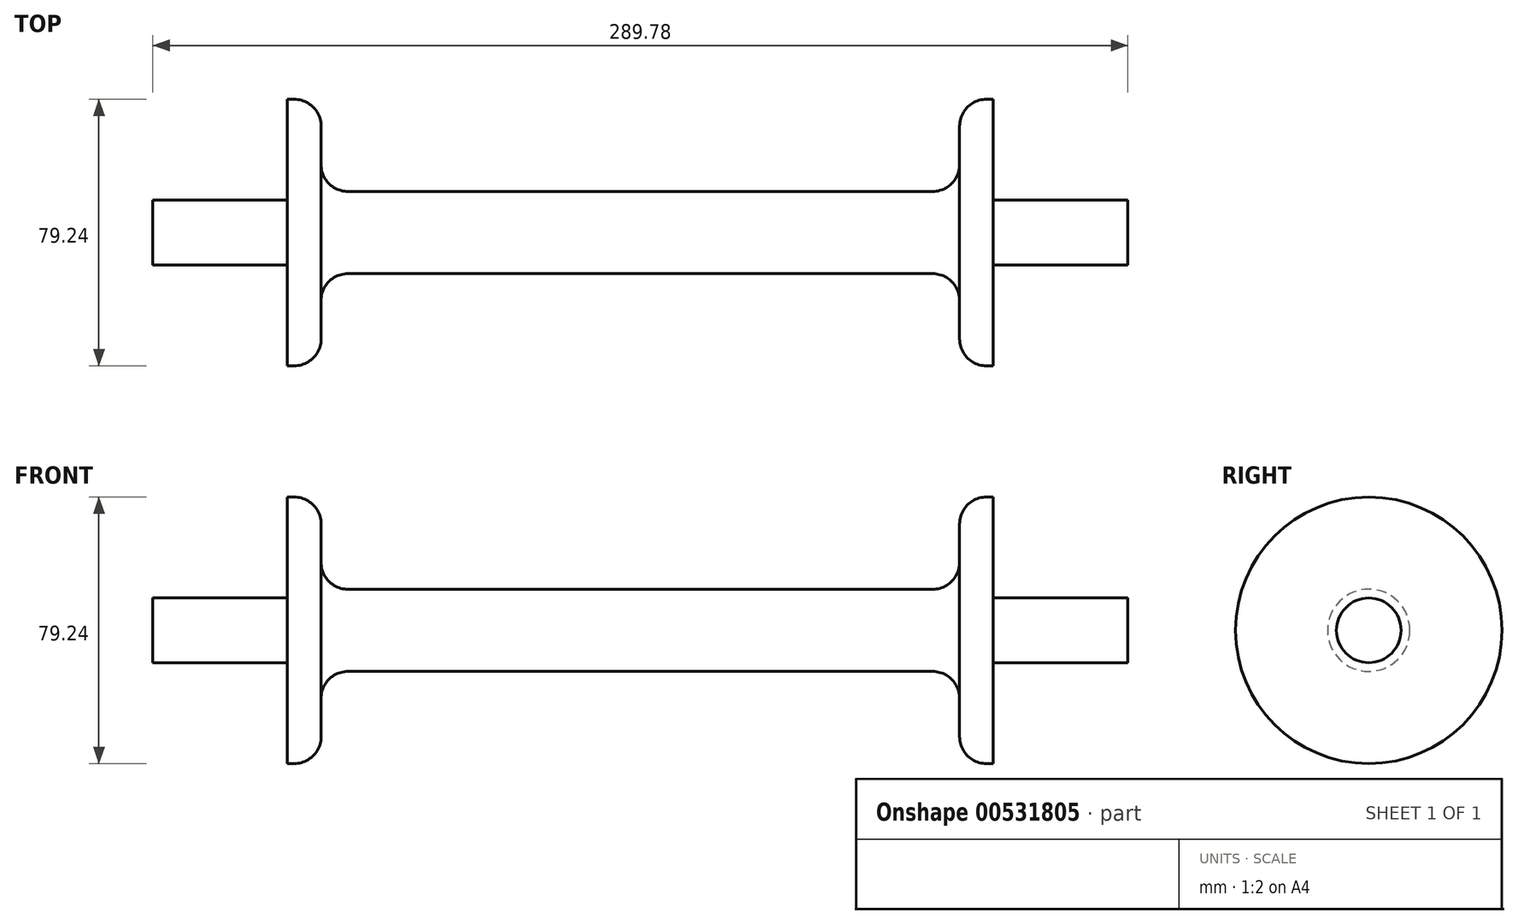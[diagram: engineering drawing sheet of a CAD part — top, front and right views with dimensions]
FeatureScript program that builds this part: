
annotation { "Feature Type Name" : "Feature", "Feature Type Description" : "" }
export const myFeature = defineFeature(function(context is Context, id is Id, definition is map)
    precondition{}
    {
        {
            var Q0;
            Q0=qCreatedBy(makeId("Front.planeOp"),FACE);
            var sketch = newSketch(context, id + "F0", { "sketchPlane" : qUnion([Q0])});
            skLineSegment(sketch, "E0", {"start": v(-5.11, 0) * mm, "end": v(144.89, 0) * mm});
            skLineSegment(sketch, "E1", {"start": v(144.89, 0) * mm, "end": v(144.89, 9.62) * mm});
            skLineSegment(sketch, "E2", {"start": v(144.89, 9.62) * mm, "end": v(104.89, 9.62) * mm});
            skLineSegment(sketch, "E3", {"start": v(104.89, 9.62) * mm, "end": v(104.89, 39.62) * mm});
            skLineSegment(sketch, "E4", {"start": v(104.89, 39.62) * mm, "end": v(102.89, 39.62) * mm});
            skLineSegment(sketch, "E5", {"start": v(94.89, 31.62) * mm, "end": v(94.89, 20.22) * mm});
            skLineSegment(sketch, "E6", {"start": v(86.89, 12.22) * mm, "end": v(-5.11, 12.22) * mm});
            skLineSegment(sketch, "E7", {"start": v(-5.11, 12.22) * mm, "end": v(-5.11, 0) * mm});
            skPoint(sketch, "E8.visualSharp", {"position": v(94.89, 12.22) * mm});
            skArc(sketch, "E8.filletArc", {"start": v(86.89, 12.22) * mm, "mid": v(92.54, 14.56) * mm, "end": v(94.89, 20.22) * mm});
            skPoint(sketch, "E9.visualSharp", {"position": v(94.89, 39.62) * mm});
            skArc(sketch, "E9.filletArc", {"start": v(102.89, 39.62) * mm, "mid": v(97.23, 37.27) * mm, "end": v(94.89, 31.62) * mm});
            skSolve(sketch);
        }
        {
            var Q0;
            Q0=makeQuery(id+"F0.imprint","IMPRINT",FACE,{"disambiguationData":[TD([[makeQuery(id+"F0.imprint","IMPRINT",EDGE,{"derivedFrom":sQuery(id+"F0.wireOp",EDGE,"E0")}),1.0]])]});
            var Q1;
            Q1=sQuery(id+"F0.wireOp",EDGE,"E0");
            revolve(context, id + "F1", {"entities" : qUnion([Q0]), "axis" : qUnion([Q1]), "revolveType" : RevolveType.FULL});
        }
        {
            var Q0;
            Q0=makeQuery(id+"F1.opRevolve","SWEPT_BODY",BODY,{"disambiguationData":[OSD([sQuery(id+"F0.wireOp",EDGE,"E0"),sQuery(id+"F0.wireOp",EDGE,"E1"),sQuery(id+"F0.wireOp",EDGE,"E2"),sQuery(id+"F0.wireOp",EDGE,"E3"),sQuery(id+"F0.wireOp",EDGE,"E4"),sQuery(id+"F0.wireOp",EDGE,"E5"),sQuery(id+"F0.wireOp",EDGE,"E6"),sQuery(id+"F0.wireOp",EDGE,"E7"),sQuery(id+"F0.wireOp",EDGE,"E8.filletArc"),sQuery(id+"F0.wireOp",EDGE,"E9.filletArc")])]});
            var Q1;
            Q1=qCreatedBy(makeId("Right.planeOp"),FACE);
            mirror(context, id + "F2", {"operationType" : NewBodyOperationType.ADD, "entities" : qUnion([Q0]), "mirrorPlane" : qUnion([Q1])});
        }
    });
